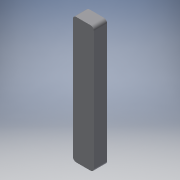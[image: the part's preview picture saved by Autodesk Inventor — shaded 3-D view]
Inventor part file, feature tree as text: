
AUTODESK INVENTOR PART (.ipt)
format: ipt  version: 2016 (Build 200138000, 138)  size: 114,176 bytes
history: native  units: in
note: dims shown in document units (in); Inventor stores cm internally (conversion verified against a paired STEP export)
features: reference x4, extrude x2, sketch x2, fillet x1
ambient origin geometry x8: Origin, YZ Plane, XZ Plane, XY Plane, X Axis, Y Axis, Z Axis, Center Point
bodies: Body1 (feature_tree)
feature tree (9):
  extrude  "Extrusion2"  Depth=0.0787in
  extrude  "Extrusion3"  Depth=0.0394in
  fillet  "Fillet2"  Radius=2.0in
  sketch  "Sketch1"  dims[d0=0.0787in d1=0.0787in]
  reference  "Reference1"
  reference  "Reference2"
  reference  "Reference3"
  reference  "Reference4"
  sketch  "Sketch2"  dims[d2=0.0787in d3=0.0787in d8=2.0in d11=0.1575in d12=0.0in d14=0.25in d15=0.5in d16=1.0in d17=0.0in d18=0.0394in]
